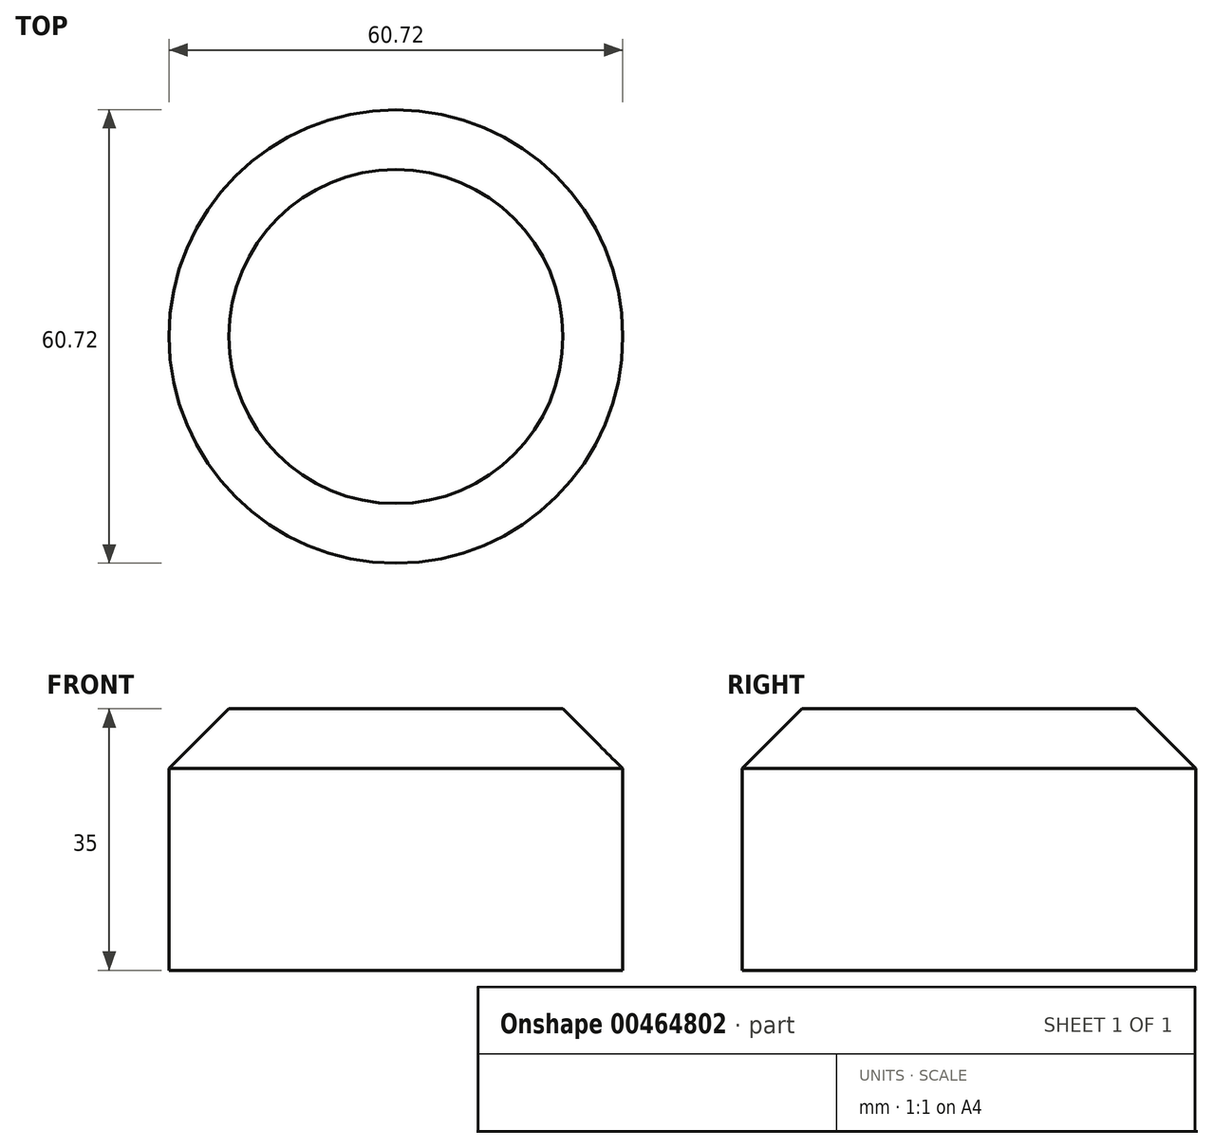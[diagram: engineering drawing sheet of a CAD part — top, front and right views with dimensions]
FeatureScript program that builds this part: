
annotation { "Feature Type Name" : "Feature", "Feature Type Description" : "" }
export const myFeature = defineFeature(function(context is Context, id is Id, definition is map)
    precondition{}
    {
        {
            var Q0;
            Q0=qCreatedBy(makeId("Top.planeOp"),FACE);
            var sketch = newSketch(context, id + "F0", { "sketchPlane" : qUnion([Q0])});
            skCircle(sketch, "E0", {"center": v(0, 0) * mm, "radius": 30.36 * mm});
            skSolve(sketch);
        }
        {
            var Q0;
            Q0=makeQuery(id+"F0.imprint","IMPRINT",FACE,{"disambiguationData":[TD([[makeQuery(id+"F0.imprint","IMPRINT",EDGE,{"derivedFrom":sQuery(id+"F0.wireOp",EDGE,"E0")}),1.0]])]});
            var Q1;
            Q1=sQuery(id+"F0.wireOp",EDGE,"E0");
            extrude(context, id + "F1", {"entities" : qUnion([Q0]), "surfaceEntities" : qUnion([Q1]), "depth" : 35 * mm});
        }
        {
            var Q0;
            Q0=makeQuery(id+"F1.opExtrude","CAP_EDGE",EDGE,{"disambiguationData":[OSD([sQuery(id+"F0.wireOp",EDGE,"E0")])],"isStart":false});
            chamfer(context, id + "F2", {"entities" : qUnion([Q0]), "width" : 8 * mm, "tangentPropagation" : true});
        }
    });
